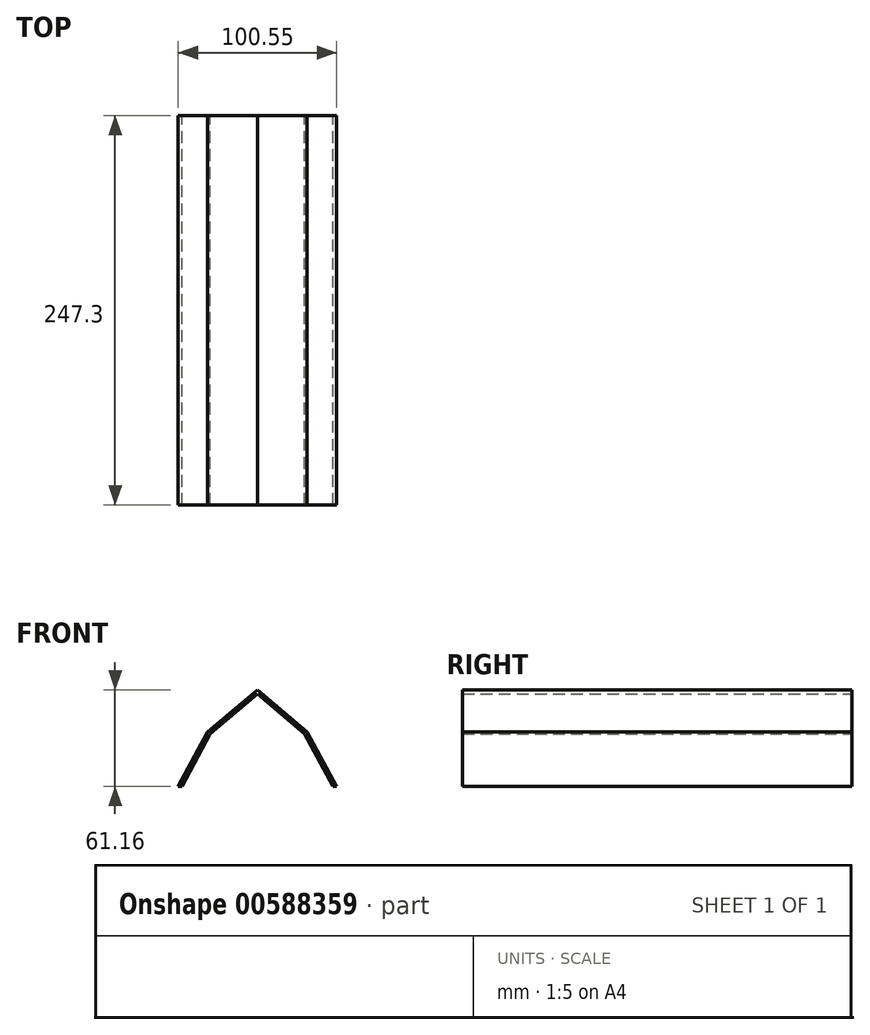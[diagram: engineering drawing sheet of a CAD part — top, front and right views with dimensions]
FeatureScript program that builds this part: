
annotation { "Feature Type Name" : "Feature", "Feature Type Description" : "" }
export const myFeature = defineFeature(function(context is Context, id is Id, definition is map)
    precondition{}
    {
        {
            var Q0;
            Q0=qCreatedBy(makeId("Front.planeOp"),FACE);
            var sketch = newSketch(context, id + "F0", { "sketchPlane" : qUnion([Q0])});
            skLineSegment(sketch, "E0", {"start": v(-85.46, 41.38) * mm, "end": v(-67.46, 8.08) * mm});
            skLineSegment(sketch, "E1", {"start": v(-115.46, 66.63) * mm, "end": v(-85.46, 41.38) * mm});
            skLineSegment(sketch, "E2", {"start": v(-115.46, 66.63) * mm, "end": v(-145.46, 41.38) * mm});
            skLineSegment(sketch, "E3", {"start": v(-163.46, 8.08) * mm, "end": v(-145.46, 41.38) * mm});
            skLineSegment(sketch, "E4.0", {"start": v(-83.88, 42.67) * mm, "end": v(-64.86, 7.48) * mm});
            skLineSegment(sketch, "E4.1", {"start": v(-115.46, 69.24) * mm, "end": v(-83.88, 42.67) * mm});
            skLineSegment(sketch, "E4.2", {"start": v(-115.46, 69.24) * mm, "end": v(-147.04, 42.67) * mm});
            skLineSegment(sketch, "E4.3", {"start": v(-166.06, 7.48) * mm, "end": v(-147.04, 42.67) * mm});
            skLineSegment(sketch, "E5", {"start": v(-163.46, 8.08) * mm, "end": v(-175.06, 8.08) * mm});
            skLineSegment(sketch, "E6", {"start": v(-175.06, 8.08) * mm, "end": v(-67.46, 8.08) * mm});
            skLineSegment(sketch, "E7", {"start": v(-67.46, 8.08) * mm, "end": v(-59.02, 8.08) * mm});
            skSolve(sketch);
        }
        {
            var Q0;
            {var subQ1=sQuery(id+"F0.wireOp",EDGE,"E0");Q0=makeQuery(id+"F0.imprint","IMPRINT",FACE,{"disambiguationData":[TD([[makeQuery(id+"F0.imprint","IMPRINT",EDGE,{"derivedFrom":subQ1}),1.0]])]});}
            extrude(context, id + "F1", {"entities" : qUnion([Q0]), "depth" : 247.3 * mm, "offsetDistance" : 25 * mm});
        }
    });
